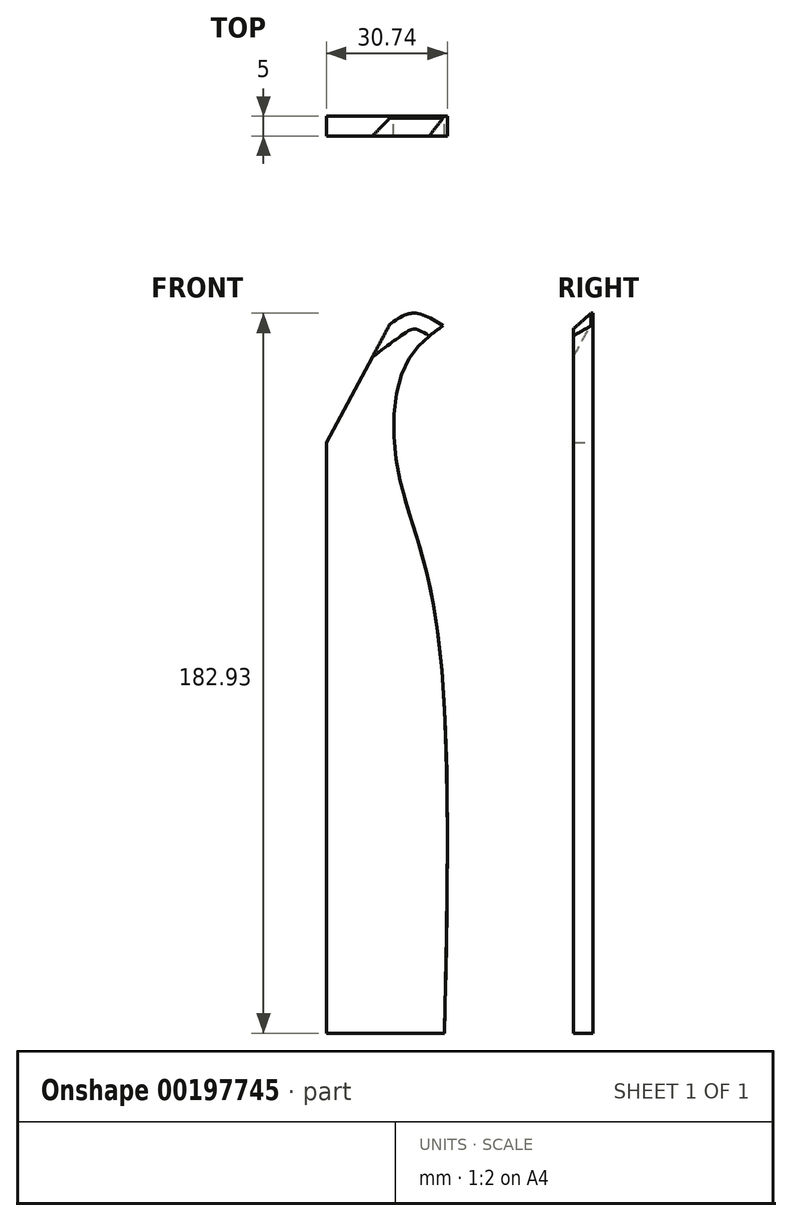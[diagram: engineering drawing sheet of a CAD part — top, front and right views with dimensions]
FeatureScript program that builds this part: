
annotation { "Feature Type Name" : "Feature", "Feature Type Description" : "" }
export const myFeature = defineFeature(function(context is Context, id is Id, definition is map)
    precondition{}
    {
        {
            var Q0;
            Q0=qCreatedBy(makeId("Front.planeOp"),FACE);
            var sketch = newSketch(context, id + "F0", { "sketchPlane" : qUnion([Q0])});
            skLineSegment(sketch, "E0", {"start": v(0, 0) * mm, "end": v(30, 0) * mm});
            skLineSegment(sketch, "E1", {"start": v(0, 0) * mm, "end": v(0, 150) * mm});
            skLineSegment(sketch, "E2", {"start": v(30, 0) * mm, "end": v(30, 180) * mm, "construction": true});
            skLineSegment(sketch, "E3", {"start": v(0, 150) * mm, "end": v(16.03, 180) * mm});
            skFitSpline(sketch, "E4", {"points": [v(30, 180) * mm, v(20.34, 170.3) * mm, v(17.75, 145.29) * mm, v(26.95, 110.23) * mm, v(30, 0) * mm], "startDerivative": vector(-74.8, -52.6) * mm, "endDerivative": vector(-6.71, -304.1) * mm});
            skFitSpline(sketch, "E5", {"points": [v(29.6, 179.72) * mm, v(22.07, 182.93) * mm, v(16.03, 180) * mm], "startDerivative": vector(-14.78, 9.35) * mm, "endDerivative": vector(-12.33, -9.09) * mm});
            skSolve(sketch);
        }
        {
            var Q0;
            {var subQ1=sQuery(id+"F0.wireOp",EDGE,"E0");Q0=makeQuery(id+"F0.imprint","IMPRINT",FACE,{"disambiguationData":[TD([[makeQuery(id+"F0.imprint","IMPRINT",EDGE,{"derivedFrom":subQ1}),1.0]])]});}
            extrude(context, id + "F1", {"entities" : qUnion([Q0]), "depth" : 5 * mm});
        }
        {
            var Q0;
            Q0=makeQuery(id+"F1.opExtrude","CAP_EDGE",EDGE,{"disambiguationData":[OSD([sQuery(id+"F0.wireOp",EDGE,"E5")])],"isStart":false});
            chamfer(context, id + "F2", {"entities" : qUnion([Q0]), "chamferType" : ChamferType.TWO_OFFSETS, "width1" : 4 * mm, "oppositeDirection" : false, "width2" : 4.5 * mm, "tangentPropagation" : true});
        }
    });
